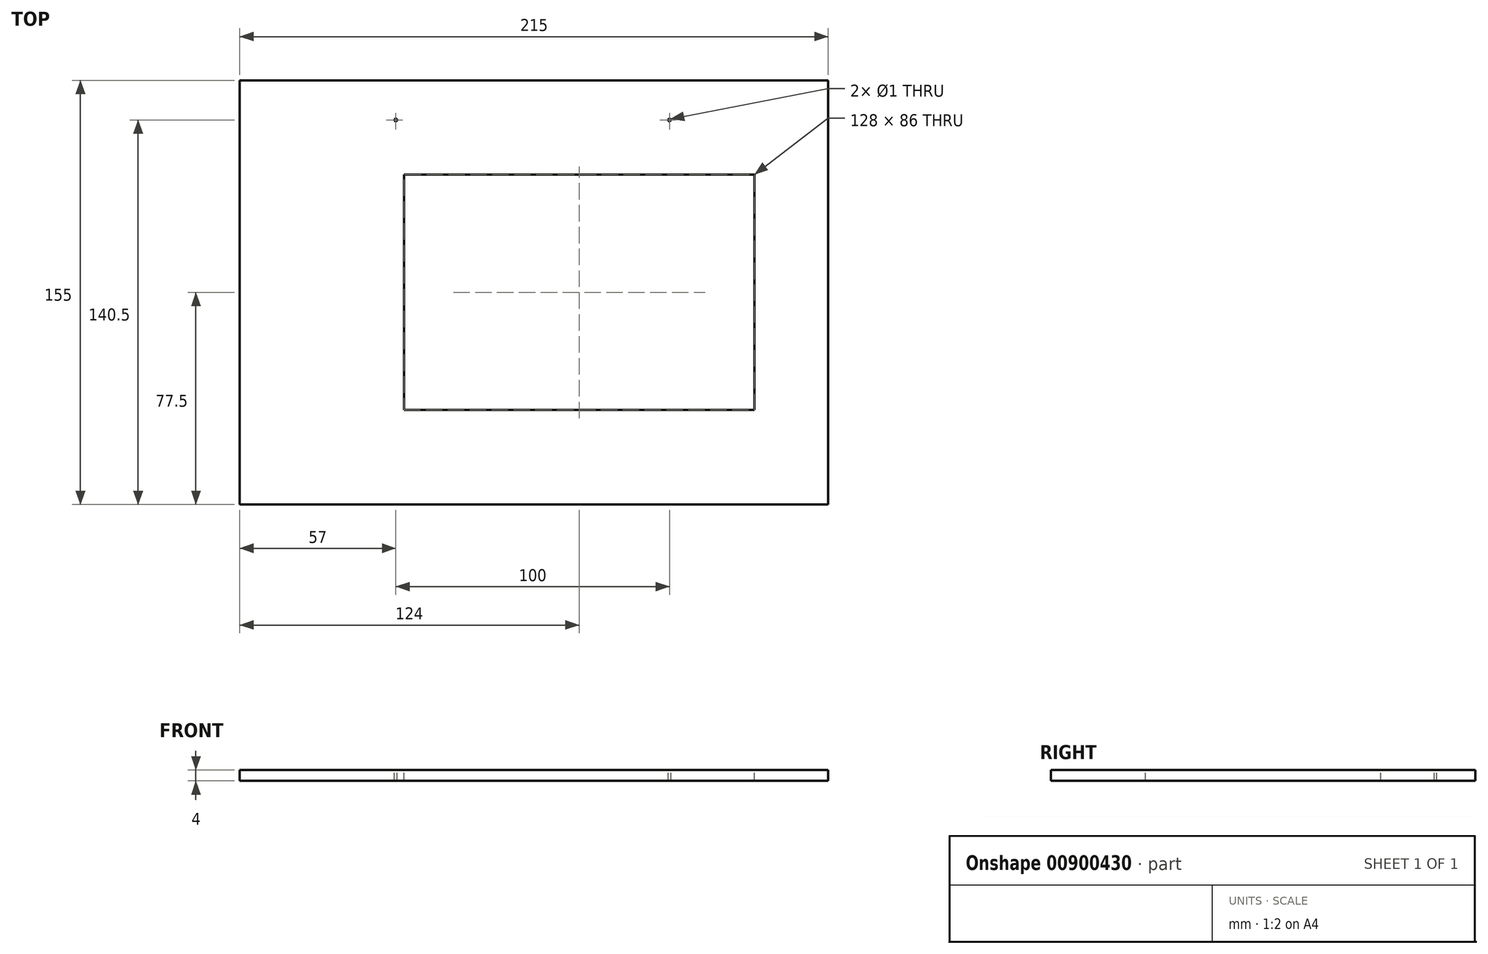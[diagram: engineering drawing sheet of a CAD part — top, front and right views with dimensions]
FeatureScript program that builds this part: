
annotation { "Feature Type Name" : "Feature", "Feature Type Description" : "" }
export const myFeature = defineFeature(function(context is Context, id is Id, definition is map)
    precondition{}
    {
        {
            var Q0;
            Q0=qCreatedBy(makeId("Top.planeOp"),FACE);
            var sketch = newSketch(context, id + "F0", { "sketchPlane" : qUnion([Q0])});
            skLineSegment(sketch, "E0.bottom", {"start": v(-107.5, 77.5) * mm, "end": v(107.5, 77.5) * mm});
            skLineSegment(sketch, "E0.top", {"start": v(-107.5, -77.5) * mm, "end": v(107.5, -77.5) * mm});
            skLineSegment(sketch, "E0.left", {"start": v(-107.5, 77.5) * mm, "end": v(-107.5, -77.5) * mm});
            skLineSegment(sketch, "E0.right", {"start": v(107.5, 77.5) * mm, "end": v(107.5, -77.5) * mm});
            skSolve(sketch);
        }
        {
            var Q0;
            Q0 = qSketchRegion(id + "F0", true);
            extrude(context, id + "F1", {"entities" : qUnion([Q0]), "depth" : 4 * mm, "offsetDistance" : 25 * mm});
        }
        {
            var Q0;
            Q0=makeQuery(id+"F1.opExtrude","CAP_FACE",FACE,{"disambiguationData":[OSD([sQuery(id+"F0.wireOp",EDGE,"E0.bottom"),sQuery(id+"F0.wireOp",EDGE,"E0.top"),sQuery(id+"F0.wireOp",EDGE,"E0.left"),sQuery(id+"F0.wireOp",EDGE,"E0.right")])],"isStart":false});
            var sketch = newSketch(context, id + "F2", { "sketchPlane" : qUnion([Q0])});
            skLineSegment(sketch, "E1", {"start": v(-155.95, 63) * mm, "end": v(145.52, 63) * mm, "construction": true});
            skCircle(sketch, "E2", {"center": v(-50.5, 63) * mm, "radius": 0.5 * mm});
            skCircle(sketch, "E3", {"center": v(49.5, 63) * mm, "radius": 0.5 * mm});
            skLineSegment(sketch, "E4.bottom", {"start": v(-47.5, 43) * mm, "end": v(80.5, 43) * mm});
            skLineSegment(sketch, "E4.top", {"start": v(-47.5, -43) * mm, "end": v(80.5, -43) * mm});
            skLineSegment(sketch, "E4.left", {"start": v(-47.5, 43) * mm, "end": v(-47.5, -43) * mm});
            skLineSegment(sketch, "E4.right", {"start": v(80.5, 43) * mm, "end": v(80.5, -43) * mm});
            skLineSegment(sketch, "E5", {"start": v(-120.16, 0) * mm, "end": v(117.5, 0) * mm, "construction": true});
            skPoint(sketch, "E5.endSnap0", {"position": v(107.5, 0) * mm});
            skSolve(sketch);
        }
        {
            var Q0;
            Q0 = qSketchRegion(id + "F2", true);
            extrude(context, id + "F3", {"entities" : qUnion([Q0]), "operationType" : NewBodyOperationType.REMOVE, "endBound" : BoundingType.THROUGH_ALL, "oppositeDirection" : true, "depth" : 25 * mm, "offsetDistance" : 25 * mm});
        }
    });
